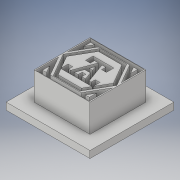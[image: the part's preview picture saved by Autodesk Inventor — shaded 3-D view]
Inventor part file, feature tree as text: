
AUTODESK INVENTOR PART (.ipt)
format: ipt  version: 2019 (Build 230136000, 136)  size: 297,984 bytes
history: native  units: mm
features: thicken_offset x10, extrude x3, sketch x3
ambient origin geometry x8: Origin, YZ Plane, XZ Plane, XY Plane, X Axis, Y Axis, Z Axis, Center Point
bodies: Solid1 (feature_tree)
feature tree (16):
  extrude  "Extrusion2"  Depth=20.0mm
  extrude  "Extrusion3"  Depth=1.0mm
  extrude  "Extrusion1"  Depth=0.1mm
  thicken_offset  "Thicken1"
  thicken_offset  "Thicken2"
  thicken_offset  "Thicken4"
  thicken_offset  "Thicken5"
  thicken_offset  "Thicken6"
  thicken_offset  "Thicken7"
  thicken_offset  "Thicken8"
  thicken_offset  "Thicken9"
  thicken_offset  "Thicken10"
  thicken_offset  "Thicken11"
  sketch  "Sketch1"  dims[d0=20.0mm d1=20.0mm]
  sketch  "Sketch2"  dims[d2=0.5mm d3=1.0mm]
  sketch  "Sketch3"  dims[d4=1.5mm d5=1.0mm d6=1.5mm d7=1.0mm d9=12.217305mm d13=1.5mm d14=1.5mm d15=1.0mm d16=1.0mm d17=2.0mm d18=1.0mm d19=2.5mm d23=1.0mm d26=2.5mm d27=10.0mm d28=0.0mm d29=0.5mm d30=1.0mm d32=1.0mm d33=1.0mm d34=1.0mm d35=30.0mm d36=30.0mm d37=2.5mm d38=0.0mm d39=20.0mm d40=20.0mm d41=10.0mm d42=0.0mm d43=0.1mm d44=1.0mm d45=0.1mm d46=0.1mm d49=0.1mm d50=0.1mm d51=0.1mm d52=0.1mm d53=0.1mm d54=0.1mm d55=0.1mm d56=0.1mm d57=0.1mm d58=0.1mm d59=0.1mm d60=0.1mm d61=0.1mm d62=0.1mm d63=0.1mm d64=0.1mm]
